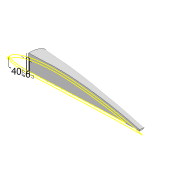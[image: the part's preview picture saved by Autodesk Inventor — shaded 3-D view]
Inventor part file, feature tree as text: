
AUTODESK INVENTOR PART (.ipt)
format: ipt  version: 2022 (Build 260153000, 153)  size: 859,136 bytes
history: native  units: mm
features: sketch x23, projected_geometry x15, extrude x12, plane x11, shell x2, chamfer x2, loft x1, fillet x1, other x1
ambient origin geometry x8: Origin, YZ Plane, XZ Plane, XY Plane, X Axis, Y Axis, Z Axis, Center Point
bodies: Solid1 (feature_tree)
feature tree (68):
  extrude  "Extrusion1"  Depth=5.0mm
  shell  "Shell1"  Thickness=6.0mm
  extrude  "Extrusion2"  Depth=2.0mm
  extrude  "Extrusion3"  Depth=5.9mm
  extrude  "Extrusion4"  Depth=10.0mm TaperAngle=0.0deg
  sketch  "Sketch29"  dims[d24=2.0mm d26=2.0mm d67=-30.0mm]
  plane  "Work Plane19"
  sketch  "Sketch28"  dims[d15=40.0mm d16=10.0mm d17=0.0mm]
  plane  "Work Plane20"
  sketch  "Sketch30"  dims[d68=-60.0mm d75=-90.0mm]
  plane  "Work Plane21"
  plane  "Work Plane22"
  plane  "Work Plane23"
  plane  "Work Plane24"
  plane  "Work Plane25"
  plane  "Work Plane26"
  plane  "Work Plane27"
  loft  "Loft7"
  extrude  "Extrusion11"  Depth=2.0mm
  shell  "Shell7"  Thickness=-30.0mm
  extrude  "Extrusion12"  [1 undecoded]
  plane  "Work Plane28"
  sketch  "Sketch45"  dims[d112=-250.0mm]
  extrude  "Extrusion13"  [1 undecoded]
  extrude  "Extrusion14"  [1 undecoded]
  extrude  "Extrusion15"  Depth=40.0mm
  extrude  "Extrusion16"  Depth=32.0mm
  extrude  "Extrusion17"  Depth=24.0mm
  chamfer  "Chamfer1"  Angle=90.0deg  [1 undecoded]
  chamfer  "Chamfer2"  Angle=90.0deg  [1 undecoded]
  fillet  "Fillet1"  [1 undecoded]
  sketch  "Sketch49"  dims[d171=0.0mm d172=90.0deg d173=0.0mm d174=90.0deg]
  plane  "Work Plane29"
  sketch  "Sketch51"  dims[d177=0.0mm d178=90.0deg d179=0.0mm d180=90.0deg d181=0.0mm d182=90.0deg d183=0.0mm d184=90.0deg d185=1000.0mm d186=0.0mm d187=1.0mm d188=1000.0mm d189=0.0mm d190=-11.0mm d191=1.0mm d192=0.0mm d193=1.0mm d194=0.0mm d195=2.1mm d196=2.1mm d197=5.9mm d198=12.0mm d199=2.8mm d200=2.8mm d201=3.0mm d202=0.0mm d203=4.0mm d204=4.0mm d205=4.0mm d206=1.25mm d207=3.25mm d208=0.0mm d209=0.0mm d210=2.0mm d211=0.0mm d212=40.0mm d213=2.0mm d214=45.0deg d215=40.0mm d216=2.0mm d217=45.0deg d218=2.0mm d219=240.0mm d220=0.0mm d222=2.95mm]
  other  "Work Axis1"
  extrude  "Extrusion18"  TaperAngle=0.0deg  [1 undecoded]
  sketch  "Sketch3"  dims[d0=4.5mm d1=0.0mm d2=5.0mm d3=6.0mm]
  sketch  "Sketch7"  dims[d5=4.5mm d6=0.0mm d7=2.0mm]
  projected_geometry  "Projected Loop3"
  sketch  "Sketch8"  dims[d8=2.0mm d9=5.9mm]
  sketch  "Sketch9"  dims[d12=4.0mm d13=10.0mm d14=0.0mm]
  sketch  "Sketch31"  dims[d76=-120.0mm d77=-150.0mm]
  sketch  "Sketch33"  dims[d78=-180.0mm d79=-210.0mm]
  sketch  "Sketch34"  dims[d80=-240.0mm d81=40.0mm]
  sketch  "Sketch35"  dims[d82=36.0mm d83=32.0mm]
  sketch  "Sketch36"  dims[d84=28.0mm d85=24.0mm]
  sketch  "Sketch37"  dims[d86=20.0mm]
  sketch  "Sketch40"  dims[d87=17.0mm]
  sketch  "Sketch43"  dims[d88=14.0mm]
  sketch  "Sketch44"  dims[d89=11.0mm]
  sketch  "Sketch46"  dims[d135=10.0mm]
  sketch  "Sketch47"  dims[d163=18.0mm]
  sketch  "Sketch48"  dims[d164=18.0mm d165=0.0mm d166=90.0deg d167=0.0mm d168=90.0deg d169=0.0mm d170=90.0deg]
  projected_geometry  "Projected Loop8"
  sketch  "Sketch50"  dims[d175=0.0mm d176=90.0deg]
  projected_geometry  "Project Cut Edges13"
  projected_geometry  "Project Cut Edges14"
  projected_geometry  "Project Cut Edges15"
  projected_geometry  "Project Cut Edges16"
  projected_geometry  "Project Cut Edges17"
  projected_geometry  "Project Cut Edges18"
  projected_geometry  "Project Cut Edges19"
  projected_geometry  "Project Cut Edges20"
  projected_geometry  "Project Cut Edges21"
  projected_geometry  "Project Cut Edges23"
  projected_geometry  "Project Cut Edges24"
  projected_geometry  "Project Cut Edges25"
  projected_geometry  "Project Cut Edges26"
note: 7 required parameter values undecoded (feature->parameter linkage not recoverable at this tier; creation-order binding heuristic only, values carry confidence <= 0.55)
